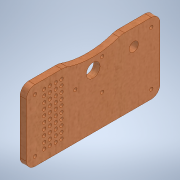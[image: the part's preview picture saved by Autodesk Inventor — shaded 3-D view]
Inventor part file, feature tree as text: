
AUTODESK INVENTOR PART (.ipt)
format: ipt  version: 2020.3 (Build 243373000, 373)  size: 240,640 bytes
history: native  units: mm
features: sketch x7, hole x4, extrude x3, fillet x2, other x1
ambient origin geometry x8: Origin, YZ Plane, XZ Plane, XY Plane, X Axis, Y Axis, Z Axis, Center Point
bodies: Body1 (feature_tree)
feature tree (17):
  other  "ソリッド1"
  extrude  "押し出し1"  Depth=61.5mm
  hole  "穴1"  [1 undecoded]
  fillet  "フィレット1"  Radius=5.5mm
  hole  "穴2"  [1 undecoded]
  hole  "穴3"  [1 undecoded]
  extrude  "押し出し2"  Depth=7.5mm
  fillet  "フィレット2"  Radius=7.5mm
  hole  "穴4"  [1 undecoded]
  extrude  "押し出し3"  Depth=7.5mm
  sketch  "スケッチ1"
  sketch  "スケッチ2"
  sketch  "スケッチ3"
  sketch  "スケッチ4"
  sketch  "スケッチ5"
  sketch  "スケッチ6"
  sketch  "スケッチ7"
note: 4 required parameter values undecoded (feature->parameter linkage not recoverable at this tier; creation-order binding heuristic only, values carry confidence <= 0.55)
